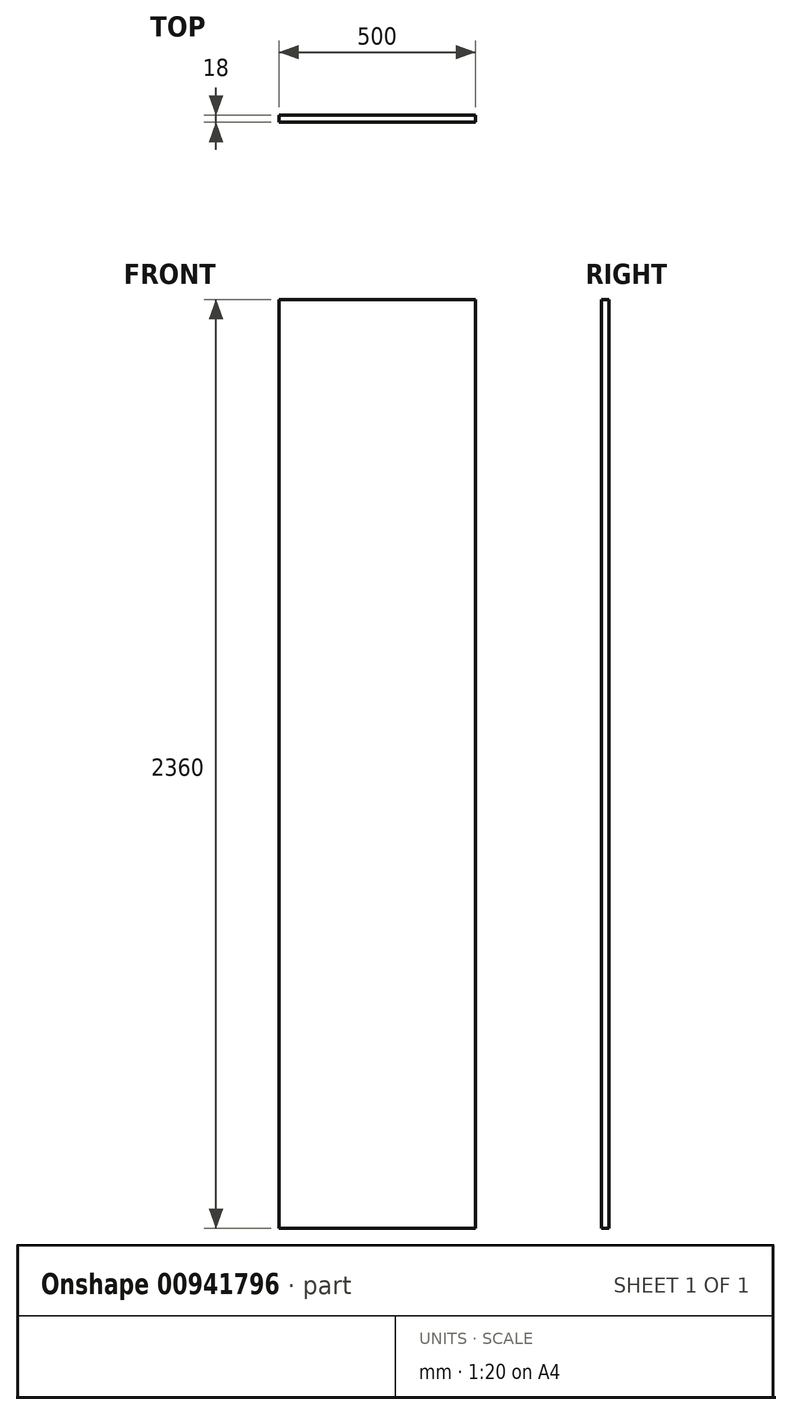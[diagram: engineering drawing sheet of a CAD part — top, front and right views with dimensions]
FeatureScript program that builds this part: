
annotation { "Feature Type Name" : "Feature", "Feature Type Description" : "" }
export const myFeature = defineFeature(function(context is Context, id is Id, definition is map)
    precondition{}
    {
        {
            var Q0;
            Q0=qCreatedBy(makeId("Front.planeOp"),FACE);
            var sketch = newSketch(context, id + "F0", { "sketchPlane" : qUnion([Q0])});
            skLineSegment(sketch, "E0.bottom", {"start": v(277.9, 1180) * mm, "end": v(-222.1, 1180) * mm});
            skLineSegment(sketch, "E0.top", {"start": v(277.9, -1180) * mm, "end": v(-222.1, -1180) * mm});
            skLineSegment(sketch, "E0.left", {"start": v(277.9, 1180) * mm, "end": v(277.9, -1180) * mm});
            skLineSegment(sketch, "E0.right", {"start": v(-222.1, 1180) * mm, "end": v(-222.1, -1180) * mm});
            skPoint(sketch, "E0.middle", {"position": v(27.9, 0) * mm});
            skSolve(sketch);
        }
        {
            var Q0;
            Q0 = qSketchRegion(id + "F0", true);
            extrude(context, id + "F1", {"entities" : qUnion([Q0]), "endBound" : BoundingType.SYMMETRIC, "depth" : 18 * mm, "offsetDistance" : 25 * mm});
        }
    });
